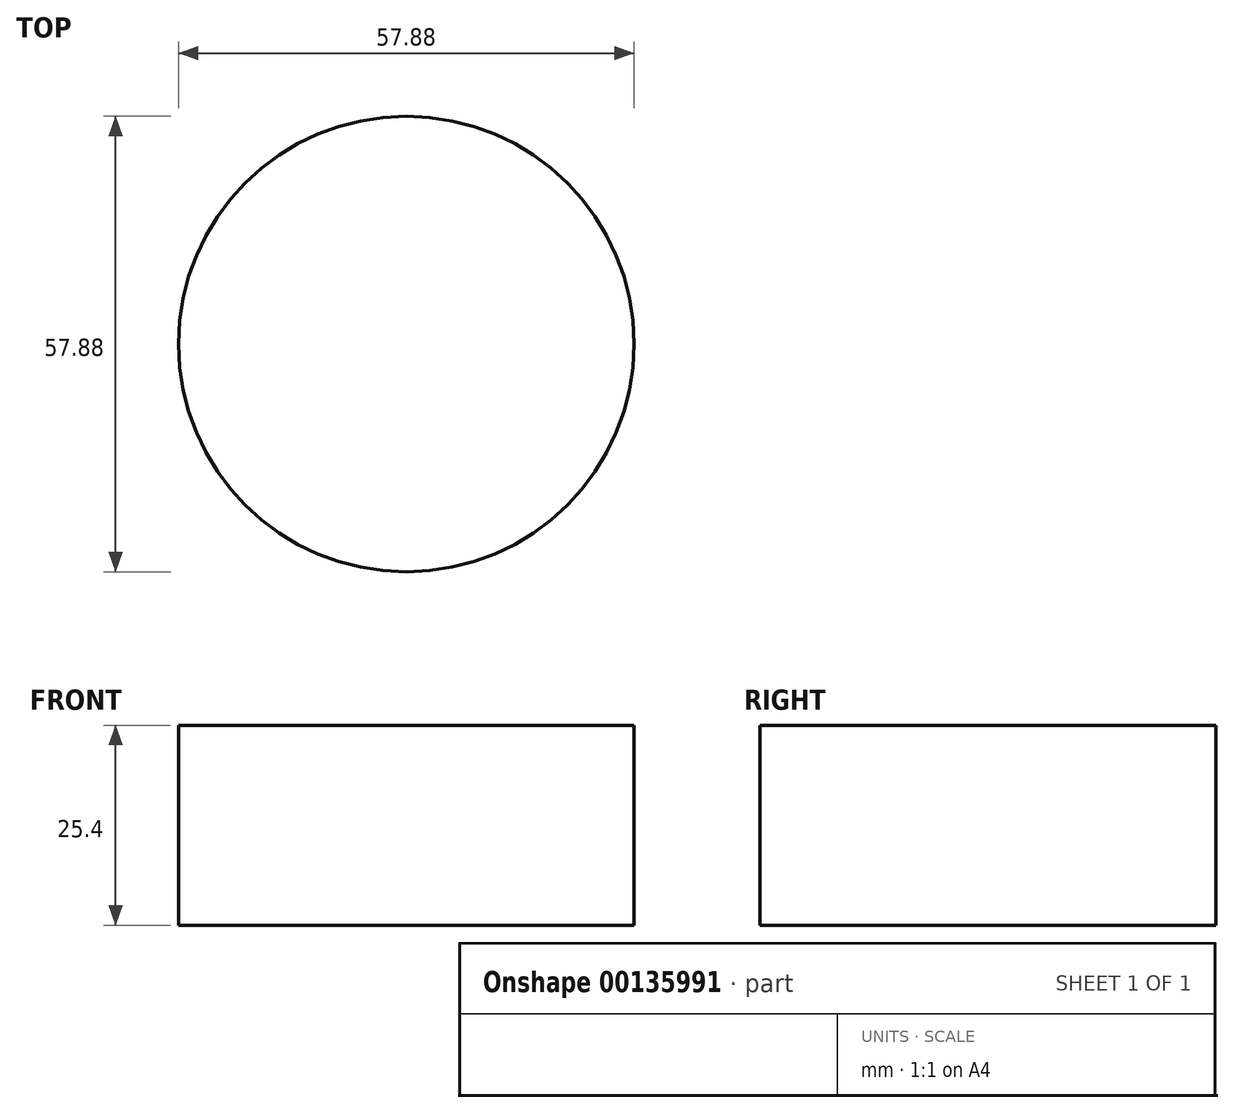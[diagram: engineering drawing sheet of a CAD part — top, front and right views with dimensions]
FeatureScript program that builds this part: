
annotation { "Feature Type Name" : "Feature", "Feature Type Description" : "" }
export const myFeature = defineFeature(function(context is Context, id is Id, definition is map)
    precondition{}
    {
        {
            var Q0;
            Q0=qCreatedBy(makeId("Top.planeOp"),FACE);
            var sketch = newSketch(context, id + "F0", { "sketchPlane" : qUnion([Q0])});
            skCircle(sketch, "E0", {"center": v(0, 0) * mm, "radius": 28.94 * mm});
            skSolve(sketch);
        }
        {
            var Q0;
            Q0=makeQuery(id+"F0.imprint","IMPRINT",FACE,{"disambiguationData":[TD([[makeQuery(id+"F0.imprint","IMPRINT",EDGE,{"derivedFrom":sQuery(id+"F0.wireOp",EDGE,"E0")}),1.0]])]});
            extrude(context, id + "F1", {"entities" : qUnion([Q0]), "depth" : 25.4 * mm});
        }
    });
